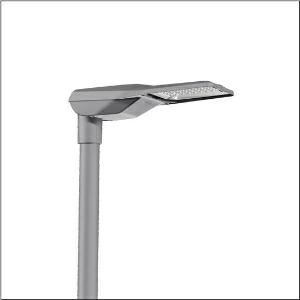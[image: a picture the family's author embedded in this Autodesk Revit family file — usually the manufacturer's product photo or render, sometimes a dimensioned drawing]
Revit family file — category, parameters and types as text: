
# Revit family: streetlight_sl_21_iq_mini___pl52_5xe2h31d08gb_8f57
name_source: partatom
category: Lighting Fixtures
units: mm (PartAtom-declared; Revit-internal decimal feet)

## family parameters
Cut with Voids When Loaded = No
Host = Face
Light Source = No
Part Type = Normal
Room Calculation Point = No
Round Connector Dimension = Use Diameter
Shared = No

## types (1)
- --- (1 x LED, 5580 lm, 37.1 W, 3000K)
    Apparent Load = 37 VA
    CIE Flux Codes = 27 59 98 100 100
    Color Rendering = 70
    Color Temperature = 3000K
    Default Elevation = 1800 mm
    Description = Streetlight SL 21 iQ mini, mast luminaire, primary light control with lens, of PMMA, primary optical cover: cover, of toughened safety glass, transparent, light distribution: PL52, light emission: direct distribution, primary light characteristic: asymmetric, installation type: post-top, side-entry, LED, High Power LED, rated luminous flux: 5.580lm, luminous efficacy: 150lm/W, light colour: 730, colour temperature: 3000K, control gear: iQ-Comfort, control: Auto-Match, Temp-Guard, Lumen-Switch, Night-Set, Smart-Wire, Light-Fading, Desk-Remote (wireless, voltage-free reading and setting of iQ features in the workshop via application-optimized NFC function/RFID function), optimised constant luminous flux control (CLO 2.0), pre-setting: linear dimming characteristic, mains connection: 220..240V, AC, 50/60Hz, start of lifetime: 37W, end of service life: 39W, reduction: 18W, luminaire housing, of diecast aluminium, powder-coated, SITECO metallic grey (DB 702S), corrosivity category C5 high according to DIN EN ISO 12944, please order mast flange separately, inclination adjustable: 0°, 5°, 10°, 15°, sealing non-destructively replaceable, multi-level sealing system, length: 628mm, width: 235mm, height: 110mm, mast flange for spigot size: 42mm (side-entry): 5XC10008XM4, 60/48mm (side-entry/post-top): 5XC10108XM2, 76/60mm (side-entry/post-top): 5XC10108XM1, mounting height: 4..8m, protection rating (complete): IP66, insulation class (complete): insulation class II (safety insulation), certification: CE, ENEC, ENEC+, VDE, impact resistance: IK10, permissible operating ambient temperature for outdoor applications: -40..+50°C, standard-compliant lighting for roads and squares, packaging unit: 1 piece

Light Distribution: PL52
    Height = 110 mm
    Lamp = 1 x LED
    Lamp Light Flux = 5580 lm
    Lamp Power = 37.1 W
    Lamp count = 1
    Length = 625 mm
    Luminous efficacy = 150 lm/W
    Manufacturer = Siteco
    ModVariant = No
    Model = 5XE2H31D08GB
    Mounting Place = Pole
    Mounting Type = Pole top
    Number of Poles = 1
    OnlyDefault = Yes
    Power Factor = 1
    Product Name = Streetlight SL 21 iQ mini | PL52
    Product group = mast luminaire | pylon top
    ProductGroupID = 6100
    Protection Class = Protection class II
    Protection Degree = IP 66
    RLX_Detail_Level = 1
    RLX_Emergency_Light_Flux = 0 lm
    RLX_Emergency_Type = 0
    RLX_Emergency_Type_DB = No
    RlxData = <blob elided: 35941 chars, md5=138409b9>
    Socket = socket
    Standby Power = 0 W
    System Light Flux = 5580 lm
    System Power = 37 W
    Type Comments = factory setting: luminous flux: 100 % | dim-lin: 254 | 385 mA
    Type Image = l_1003519.jpg
    URL = http://relux.com
    VarID = @adj_189377
    Voltage = 0 V
    Weight = 0.00 kg
    Width = 234 mm

## geometry (parser evidence)
native form markers: Blend x4, Sweep x11
no freeform markers — native parametric forms only
